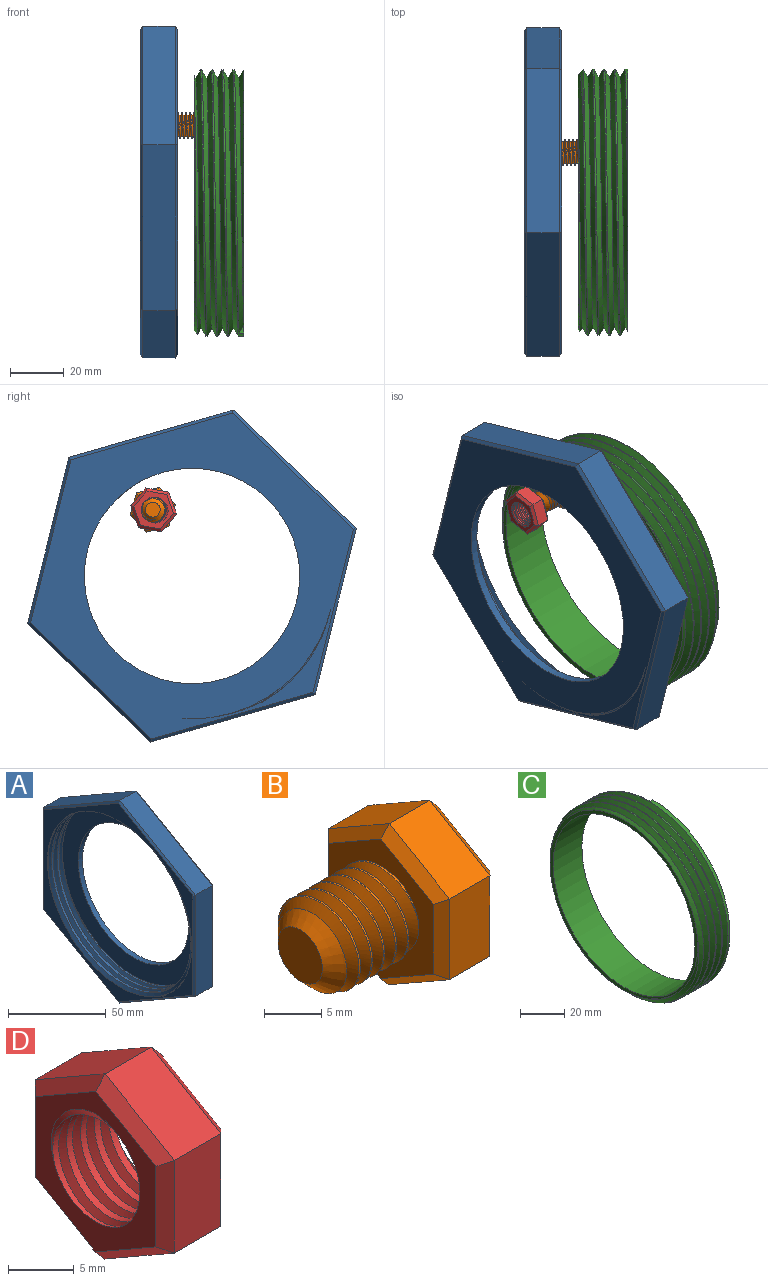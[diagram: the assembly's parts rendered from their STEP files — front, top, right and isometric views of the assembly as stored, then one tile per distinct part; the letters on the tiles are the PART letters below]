
ASSEMBLY  parts=4 mates=2
PART A: 26 faces, bbox 18.9x125.5x128.7 mm
  f0: cylinder r=51.39mm len=102.79mm, axis (1,0,0), area 1243.5mm2, adj f7,f21,f22,f24
  f1: plane 54.98x31.79mm, normal (0,-0.5,0.87), area 762.1mm2, adj f2,f6,f14,f18
  f2: plane 63.51x12mm, normal (0,-1,0), area 762.1mm2, adj f1,f3,f12,f16
  f3: plane 55.02x31.72mm, normal (0,-0.5,-0.87), area 762.1mm2, adj f2,f4,f10,f15
  f4: plane 54.98x31.79mm, normal (0,0.5,-0.87), area 762.1mm2, adj f3,f5,f9,f17
  f5: plane 63.51x12mm, normal (0,1,0), area 762.1mm2, adj f4,f6,f11,f19
  f6: plane 55.02x31.72mm, normal (0,0.5,0.87), area 762.1mm2, adj f1,f5,f13,f20
  f7: plane 126.37x109.7mm, normal (-1,0,0), area 1563.5mm2, adj f0,f9,f10,f11,f12,f13,f14,f21
  f8: plane 125.33x108.66mm, normal (1,0,0), area 5054.4mm2, adj f15,f16,f17,f18,f19,f20,f21,f22
  f9: plane 54.98x32.37mm, normal (-0.71,0.35,-0.61), area 89mm2, adj f4,f7,f10,f11
  f10: plane 55.02x32.3mm, normal (-0.71,-0.35,-0.61), area 89mm2, adj f3,f7,f9,f12
  f11: plane 63.51x1.04mm, normal (-0.71,0.71,0), area 89mm2, adj f5,f7,f9,f13
  f12: plane 63.51x1.04mm, normal (-0.71,-0.71,0), area 89mm2, adj f2,f7,f10,f14
  f13: plane 55.02x32.3mm, normal (-0.71,0.35,0.61), area 89mm2, adj f6,f7,f11,f14
  f14: plane 54.98x32.37mm, normal (-0.71,-0.35,0.61), area 89mm2, adj f1,f7,f12,f13
  f15: plane 55.02x32.3mm, normal (0.71,-0.35,-0.61), area 89mm2, adj f3,f8,f16,f17
  f16: plane 63.51x1.04mm, normal (0.71,-0.71,0), area 89mm2, adj f2,f8,f15,f18
  f17: plane 54.98x32.37mm, normal (0.71,0.35,-0.61), area 89mm2, adj f4,f8,f15,f19
  f18: plane 54.98x32.37mm, normal (0.71,-0.35,0.61), area 89mm2, adj f1,f8,f16,f20
  f19: plane 63.51x1.04mm, normal (0.71,0.71,0), area 89mm2, adj f5,f8,f17,f20
  f20: plane 55.02x32.3mm, normal (0.71,0.35,0.61), area 89mm2, adj f6,f8,f18,f19
  f21: bspline ~123.89x107.29mm, area 2546.2mm2, adj f0,f7,f8,f22,f23,f24
  f22: bspline ~123.89x107.29mm, area 2544.2mm2, adj f0,f7,f8,f21,f23,f24
  f23: cylinder r=53mm len=106mm, axis (1,0,0), area 186.2mm2, adj f8,f21,f22,f24
  f24: plane 105.72x105.19mm, normal (-1,0,0), area 3491.4mm2, adj f0,f21,f22,f23,f25
  f25: cylinder r=40mm len=80mm, axis (1,0,0), area 754mm2, adj f8,f24
PART B: 25 faces, bbox 17.8x15.9x18.1 mm
  f0: cylinder r=4.75mm len=9.5mm, axis (1,0,0), area 28.1mm2, adj f1,f2,f4,f12
  f1: bspline ~10.97x9.91mm, area 196.7mm2, adj f0,f2,f4,f12
  f2: bspline ~10.97x10.66mm, area 196.6mm2, adj f0,f1,f4,f12
  f3: plane 5.5x5.5mm, normal (-1,0,0), area 23.8mm2, adj f4
  f4: cone r=4.75mm half-angle=45deg, axis (1,0,0), area 47.4mm2, adj f0,f1,f2,f3
  f5: plane 7.48x5mm, normal (0,-0.5,0.86), area 43.3mm2, adj f6,f10,f18,f22
  f6: plane 8.66x5mm, normal (0,-1,0), area 43.3mm2, adj f5,f7,f16,f20
  f7: plane 7.52x5mm, normal (0,-0.5,-0.87), area 43.3mm2, adj f6,f8,f14,f19
  f8: plane 7.48x5mm, normal (0,0.5,-0.86), area 43.3mm2, adj f7,f9,f13,f21
  f9: plane 8.66x5mm, normal (0,1,0), area 43.3mm2, adj f8,f10,f15,f23
  f10: plane 7.52x5mm, normal (0,0.5,0.87), area 43.3mm2, adj f5,f9,f17,f24
  f11: plane 15.01x13.03mm, normal (1,0,0), area 146.4mm2, adj f13,f14,f15,f16,f17,f18
  f12: plane 15.83x13.85mm, normal (-1,0,0), area 89.2mm2, adj f0,f1,f2,f19,f20,f21,f22,f23
  f13: plane 7.49x4.93mm, normal (0.71,0.36,-0.61), area 11.4mm2, adj f8,f11,f14,f15
  f14: plane 7.52x4.88mm, normal (0.71,-0.35,-0.61), area 11.4mm2, adj f7,f11,f13,f16
  f15: plane 8.66x1.03mm, normal (0.71,0.71,0), area 11.4mm2, adj f9,f11,f13,f17
  f16: plane 8.66x1.03mm, normal (0.71,-0.71,0), area 11.4mm2, adj f6,f11,f14,f18
  f17: plane 7.52x4.88mm, normal (0.71,0.35,0.61), area 11.4mm2, adj f10,f11,f15,f18
  f18: plane 7.49x4.93mm, normal (0.71,-0.36,0.61), area 11.4mm2, adj f5,f11,f16,f17
  f19: plane 7.52x4.88mm, normal (-0.71,-0.35,-0.61), area 11.4mm2, adj f7,f12,f20,f21
  f20: plane 8.66x1.03mm, normal (-0.71,-0.71,0), area 11.4mm2, adj f6,f12,f19,f22
  f21: plane 7.49x4.93mm, normal (-0.71,0.36,-0.61), area 11.4mm2, adj f8,f12,f19,f23
  f22: plane 7.49x4.93mm, normal (-0.71,-0.36,0.61), area 11.4mm2, adj f5,f12,f20,f24
  f23: plane 8.66x1.03mm, normal (-0.71,0.71,0), area 11.4mm2, adj f9,f12,f21,f24
  f24: plane 7.52x4.88mm, normal (-0.71,0.35,0.61), area 11.4mm2, adj f10,f12,f22,f23
PART C: 8 faces, bbox 24.8x116.8x101.6 mm
  f0: cylinder r=49.44mm len=98.88mm, axis (1,0,0), area 776.6mm2, adj f2,f3,f4,f5,f6
  f1: plane 95.81x95.8mm, normal (-1,0,0), area 521mm2, adj f3,f4,f5,f7
  f2: plane 101.55x100.27mm, normal (1,0,0), area 973.5mm2, adj f0,f4,f6,f7
  f3: cone r=49.44mm half-angle=45deg, axis (1,0,0), area 354.4mm2, adj f0,f1,f4,f5
  f4: bspline ~114.18x98.88mm, area 4694.9mm2, adj f0,f1,f2,f3,f5
  f5: bspline ~114.18x98.88mm, area 4465.5mm2, adj f0,f1,f3,f4,f6
  f6: plane 3.03x1.75mm, normal (0,1,0), area 2.7mm2, adj f0,f2,f5
  f7: cylinder r=45.5mm len=91mm, axis (1,0,0), area 5288.9mm2, adj f1,f2
PART D: 23 faces, bbox 9.1x15.4x17.7 mm
  f0: plane 7.49x5mm, normal (0,-0.5,0.86), area 43.3mm2, adj f1,f5,f13,f17
  f1: plane 8.66x5mm, normal (0,-1,0), area 43.3mm2, adj f0,f2,f11,f15
  f2: plane 7.51x5mm, normal (0,-0.5,-0.87), area 43.3mm2, adj f1,f3,f9,f14
  f3: plane 7.49x5mm, normal (0,0.5,-0.86), area 43.3mm2, adj f2,f4,f8,f16
  f4: plane 8.66x5mm, normal (0,1,0), area 43.3mm2, adj f3,f5,f10,f18
  f5: plane 7.51x5mm, normal (0,0.5,0.87), area 43.3mm2, adj f0,f4,f12,f19
  f6: plane 15.37x13.38mm, normal (-1,0,0), area 71.4mm2, adj f8,f9,f10,f11,f12,f13,f20,f21
  f7: plane 15.37x13.38mm, normal (1,0,0), area 71.4mm2, adj f14,f15,f16,f17,f18,f19,f20,f21
  f8: plane 7.49x4.93mm, normal (-0.71,0.36,-0.61), area 11.4mm2, adj f3,f6,f9,f10
  f9: plane 7.51x4.89mm, normal (-0.71,-0.35,-0.61), area 11.4mm2, adj f2,f6,f8,f11
  f10: plane 8.66x1.02mm, normal (-0.71,0.71,0), area 11.4mm2, adj f4,f6,f8,f12
  f11: plane 8.66x1.02mm, normal (-0.71,-0.71,0), area 11.4mm2, adj f1,f6,f9,f13
  f12: plane 7.51x4.89mm, normal (-0.71,0.35,0.61), area 11.4mm2, adj f5,f6,f10,f13
  f13: plane 7.49x4.93mm, normal (-0.71,-0.36,0.61), area 11.4mm2, adj f0,f6,f11,f12
  f14: plane 7.51x4.89mm, normal (0.71,-0.35,-0.61), area 11.4mm2, adj f2,f7,f15,f16
  f15: plane 8.66x1.02mm, normal (0.71,-0.71,0), area 11.4mm2, adj f1,f7,f14,f17
  f16: plane 7.49x4.93mm, normal (0.71,0.36,-0.61), area 11.4mm2, adj f3,f7,f14,f18
  f17: plane 7.49x4.93mm, normal (0.71,-0.36,0.61), area 11.4mm2, adj f0,f7,f15,f19
  f18: plane 8.66x1.02mm, normal (0.71,0.71,0), area 11.4mm2, adj f4,f7,f16,f19
  f19: plane 7.51x4.89mm, normal (0.71,0.35,0.61), area 11.4mm2, adj f5,f7,f17,f18
  f20: cylinder r=4.66mm len=9.32mm, axis (1,0,0), area 85.4mm2, adj f6,f7,f21,f22
  f21: bspline ~12.5x10.82mm, area 128.4mm2, adj f6,f7,f20,f22
  f22: bspline ~12.5x10.82mm, area 128.5mm2, adj f6,f7,f20,f21
PLACE A rot(axis=(0,0.6,-0.8),180deg) t=(-55.27,-6.86,23.48)mm fixed
PLACE B rot(axis=(-1,0,0),43.8deg) t=(-31.66,7.73,48.08)mm
PLACE C rot(axis=(1,0,0),167.5deg) t=(-16.77,-10.68,19.38)mm
PLACE D rot(axis=(1,0,0),100.2deg) t=(-48.16,7.38,48.02)mm fixed
MATE cylindrical C.f0 <-> A.f7  axis (-1,0,0) through (-35.27,-10.68,19.38)mm
MATE cylindrical B.f0 <-> D.f6  axis (-1,0,0) through (-45.16,7.73,48.08)mm
